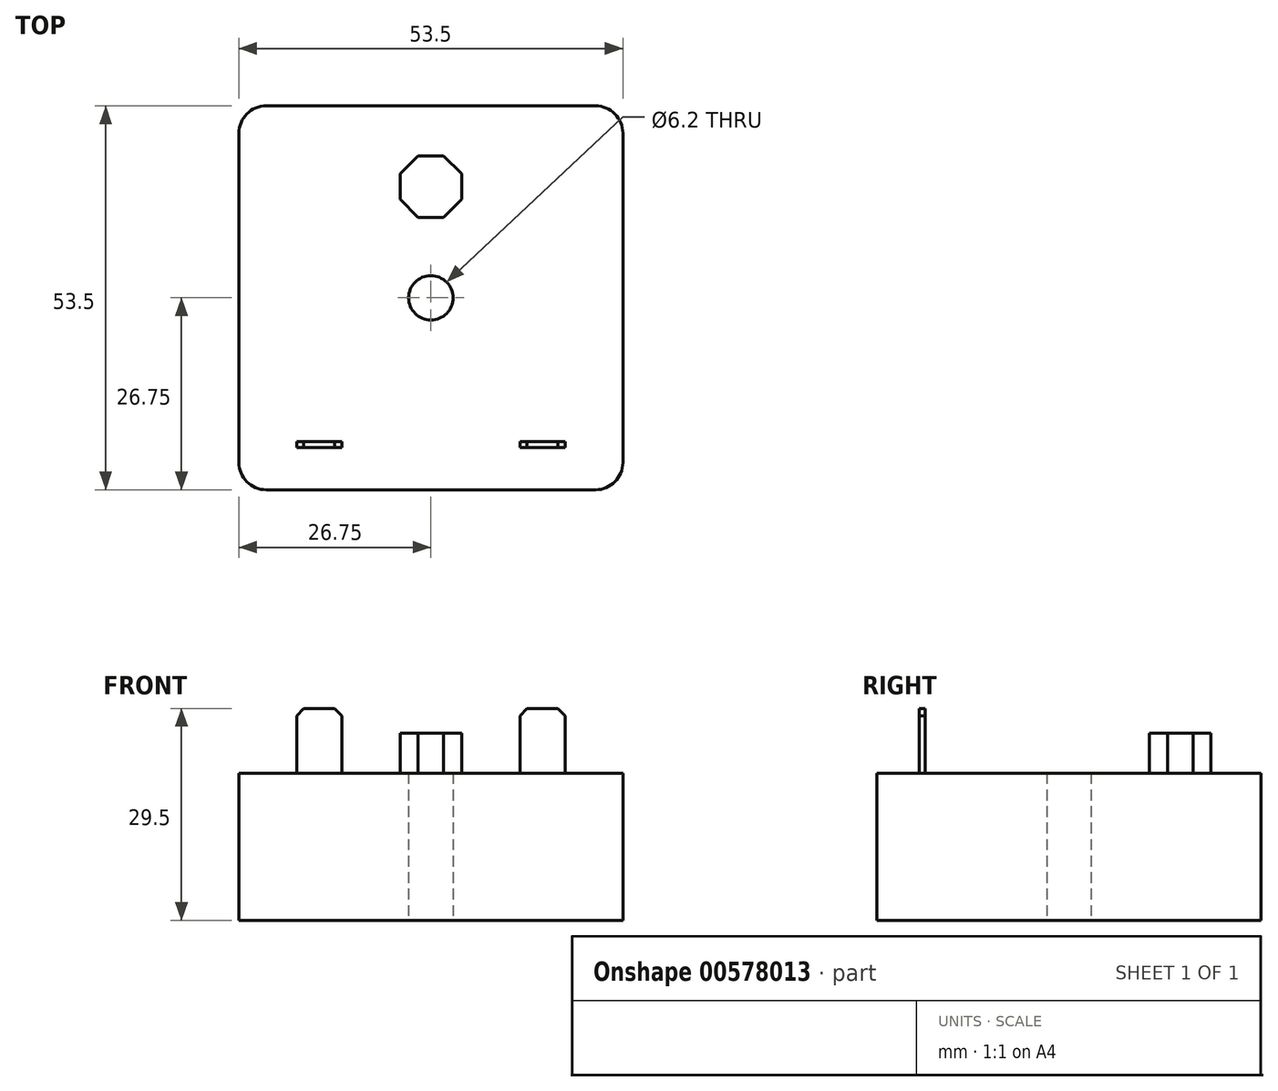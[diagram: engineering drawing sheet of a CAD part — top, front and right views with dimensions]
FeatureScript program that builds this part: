
annotation { "Feature Type Name" : "Feature", "Feature Type Description" : "" }
export const myFeature = defineFeature(function(context is Context, id is Id, definition is map)
    precondition{}
    {
        {
            var Q0;
            Q0=qCreatedBy(makeId("Top.planeOp"),FACE);
            var sketch = newSketch(context, id + "F0", { "sketchPlane" : qUnion([Q0])});
            skLineSegment(sketch, "E0.bottom", {"start": v(22.95, -26.75) * mm, "end": v(-22.95, -26.75) * mm});
            skLineSegment(sketch, "E0.top", {"start": v(22.95, 26.75) * mm, "end": v(-22.95, 26.75) * mm});
            skLineSegment(sketch, "E0.left", {"start": v(26.75, -22.95) * mm, "end": v(26.75, 22.95) * mm});
            skLineSegment(sketch, "E0.right", {"start": v(-26.75, -22.95) * mm, "end": v(-26.75, 22.95) * mm});
            skPoint(sketch, "E0.middle", {"position": v(0, 0) * mm});
            skLineSegment(sketch, "E1", {"start": v(-26.75, -26.75) * mm, "end": v(26.75, 26.75) * mm, "construction": true});
            skPoint(sketch, "E2", {"position": v(-25.63, -25.63) * mm});
            skPoint(sketch, "E3.visualSharp", {"position": v(-26.75, -26.75) * mm});
            skArc(sketch, "E3.filletArc", {"start": v(-26.75, -22.95) * mm, "mid": v(-25.64, -25.64) * mm, "end": v(-22.95, -26.75) * mm});
            skPoint(sketch, "E4.visualSharp", {"position": v(26.75, -26.75) * mm});
            skArc(sketch, "E4.filletArc", {"start": v(22.95, -26.75) * mm, "mid": v(25.64, -25.64) * mm, "end": v(26.75, -22.95) * mm});
            skPoint(sketch, "E5.visualSharp", {"position": v(26.75, 26.75) * mm});
            skArc(sketch, "E5.filletArc", {"start": v(26.75, 22.95) * mm, "mid": v(25.64, 25.64) * mm, "end": v(22.95, 26.75) * mm});
            skPoint(sketch, "E6.visualSharp", {"position": v(-26.75, 26.75) * mm});
            skArc(sketch, "E6.filletArc", {"start": v(-22.95, 26.75) * mm, "mid": v(-25.64, 25.64) * mm, "end": v(-26.75, 22.95) * mm});
            skCircle(sketch, "E7", {"center": v(0, 0) * mm, "radius": 3.1 * mm});
            skSolve(sketch);
        }
        {
            var Q0;
            Q0 = qSketchRegion(id + "F0", true);
            extrude(context, id + "F1", {"entities" : qUnion([Q0]), "depth" : 20.5 * mm, "offsetDistance" : 25 * mm});
        }
        {
            var Q0;
            Q0=makeQuery(id+"F1.opExtrude","CAP_FACE",FACE,{"disambiguationData":[OSD([sQuery(id+"F0.wireOp",EDGE,"E0.bottom"),sQuery(id+"F0.wireOp",EDGE,"E0.top"),sQuery(id+"F0.wireOp",EDGE,"E0.left"),sQuery(id+"F0.wireOp",EDGE,"E0.right"),sQuery(id+"F0.wireOp",EDGE,"E3.filletArc"),sQuery(id+"F0.wireOp",EDGE,"E4.filletArc"),sQuery(id+"F0.wireOp",EDGE,"E5.filletArc"),sQuery(id+"F0.wireOp",EDGE,"E6.filletArc"),sQuery(id+"F0.wireOp",EDGE,"E7")])],"isStart":false});
            var sketch = newSketch(context, id + "F2", { "sketchPlane" : qUnion([Q0])});
            skCircle(sketch, "E8.cCircle", {"center": v(0, 15.5) * mm, "radius": 4.3 * mm, "construction": true});
            skLineSegment(sketch, "E8.0", {"start": v(4.3, 17.28) * mm, "end": v(4.3, 13.72) * mm});
            skLineSegment(sketch, "E8.1", {"start": v(4.3, 13.72) * mm, "end": v(1.78, 11.2) * mm});
            skLineSegment(sketch, "E8.2", {"start": v(1.78, 11.2) * mm, "end": v(-1.78, 11.2) * mm});
            skLineSegment(sketch, "E8.3", {"start": v(-1.78, 11.2) * mm, "end": v(-4.3, 13.72) * mm});
            skLineSegment(sketch, "E8.4", {"start": v(-4.3, 13.72) * mm, "end": v(-4.3, 17.28) * mm});
            skLineSegment(sketch, "E8.5", {"start": v(-4.3, 17.28) * mm, "end": v(-1.78, 19.8) * mm});
            skLineSegment(sketch, "E8.6", {"start": v(-1.78, 19.8) * mm, "end": v(1.78, 19.8) * mm});
            skLineSegment(sketch, "E8.7", {"start": v(1.78, 19.8) * mm, "end": v(4.3, 17.28) * mm});
            skPoint(sketch, "E8.0.midPoint", {"position": v(4.3, 15.5) * mm});
            skSolve(sketch);
        }
        {
            var Q0;
            Q0 = qSketchRegion(id + "F2", true);
            extrude(context, id + "F3", {"entities" : qUnion([Q0]), "operationType" : NewBodyOperationType.ADD, "depth" : 5.6 * mm, "offsetDistance" : 25 * mm});
        }
        {
            var Q0;
            Q0=makeQuery(id+"F1.opExtrude","CAP_FACE",FACE,{"disambiguationData":[OSD([sQuery(id+"F0.wireOp",EDGE,"E0.bottom"),sQuery(id+"F0.wireOp",EDGE,"E0.top"),sQuery(id+"F0.wireOp",EDGE,"E0.left"),sQuery(id+"F0.wireOp",EDGE,"E0.right"),sQuery(id+"F0.wireOp",EDGE,"E3.filletArc"),sQuery(id+"F0.wireOp",EDGE,"E4.filletArc"),sQuery(id+"F0.wireOp",EDGE,"E5.filletArc"),sQuery(id+"F0.wireOp",EDGE,"E6.filletArc"),sQuery(id+"F0.wireOp",EDGE,"E7")])],"isStart":false});
            var sketch = newSketch(context, id + "F4", { "sketchPlane" : qUnion([Q0])});
            skLineSegment(sketch, "E9.bottom", {"start": v(-12.4, -20.85) * mm, "end": v(-18.7, -20.85) * mm});
            skLineSegment(sketch, "E9.top", {"start": v(-12.4, -20.05) * mm, "end": v(-18.7, -20.05) * mm});
            skLineSegment(sketch, "E9.left", {"start": v(-12.4, -20.85) * mm, "end": v(-12.4, -20.05) * mm});
            skLineSegment(sketch, "E9.right", {"start": v(-18.7, -20.85) * mm, "end": v(-18.7, -20.05) * mm});
            skPoint(sketch, "E9.middle", {"position": v(-15.55, -20.45) * mm});
            skLineSegment(sketch, "E10.MirrorCS", {"start": v(12.4, -20.05) * mm, "end": v(18.7, -20.05) * mm});
            skLineSegment(sketch, "E11.MirrorCS", {"start": v(18.7, -20.85) * mm, "end": v(18.7, -20.05) * mm});
            skLineSegment(sketch, "E12.MirrorCS", {"start": v(12.4, -20.85) * mm, "end": v(18.7, -20.85) * mm});
            skLineSegment(sketch, "E13.MirrorCS", {"start": v(12.4, -20.85) * mm, "end": v(12.4, -20.05) * mm});
            skSolve(sketch);
        }
        {
            var Q0;
            Q0 = qSketchRegion(id + "F4", true);
            extrude(context, id + "F5", {"entities" : qUnion([Q0]), "operationType" : NewBodyOperationType.ADD, "depth" : 9 * mm, "offsetDistance" : 25 * mm});
        }
        {
            var Q0;
            Q0=makeQuery(id+"F5.opExtrude","CAP_EDGE",EDGE,{"disambiguationData":[OSD([sQuery(id+"F4.wireOp",EDGE,"E9.right")])],"isStart":false});
            var Q1;
            Q1=makeQuery(id+"F5.opExtrude","CAP_EDGE",EDGE,{"disambiguationData":[OSD([sQuery(id+"F4.wireOp",EDGE,"E9.left")])],"isStart":false});
            var Q2;
            Q2=makeQuery(id+"F5.opExtrude","CAP_EDGE",EDGE,{"disambiguationData":[OSD([sQuery(id+"F4.wireOp",EDGE,"E13.MirrorCS")])],"isStart":false});
            var Q3;
            Q3=makeQuery(id+"F5.opExtrude","CAP_EDGE",EDGE,{"disambiguationData":[OSD([sQuery(id+"F4.wireOp",EDGE,"E11.MirrorCS")])],"isStart":false});
            chamfer(context, id + "F6", {"entities" : qUnion([Q0, Q1, Q2, Q3]), "width" : 1 * mm, "tangentPropagation" : true});
        }
    });
